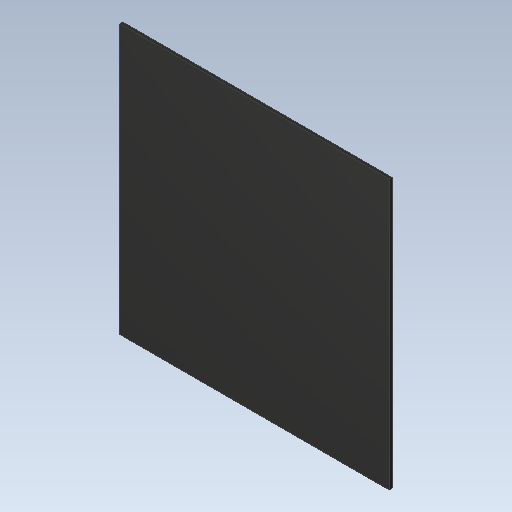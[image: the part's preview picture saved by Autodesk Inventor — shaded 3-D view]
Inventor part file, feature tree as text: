
AUTODESK INVENTOR PART (.ipt)
format: ipt  version: 2020 (Build 240168000, 168)  size: 86,016 bytes
history: imported  units: in
note: dims shown in document units (in); Inventor stores cm internally (conversion verified against a paired STEP export)
features: imported_body x1
ambient origin geometry x8: Origin, YZ Plane, XZ Plane, XY Plane, X Axis, Y Axis, Z Axis, Center Point
bodies: Solid1 (imported_parasolid), Body1 (imported_parasolid)
feature tree (1):
  imported_body  NMx_Import_Brep_tag  [imported B-rep: ~6 faces, bbox_mm=[9.8552, 9.8552, 0.1]]
